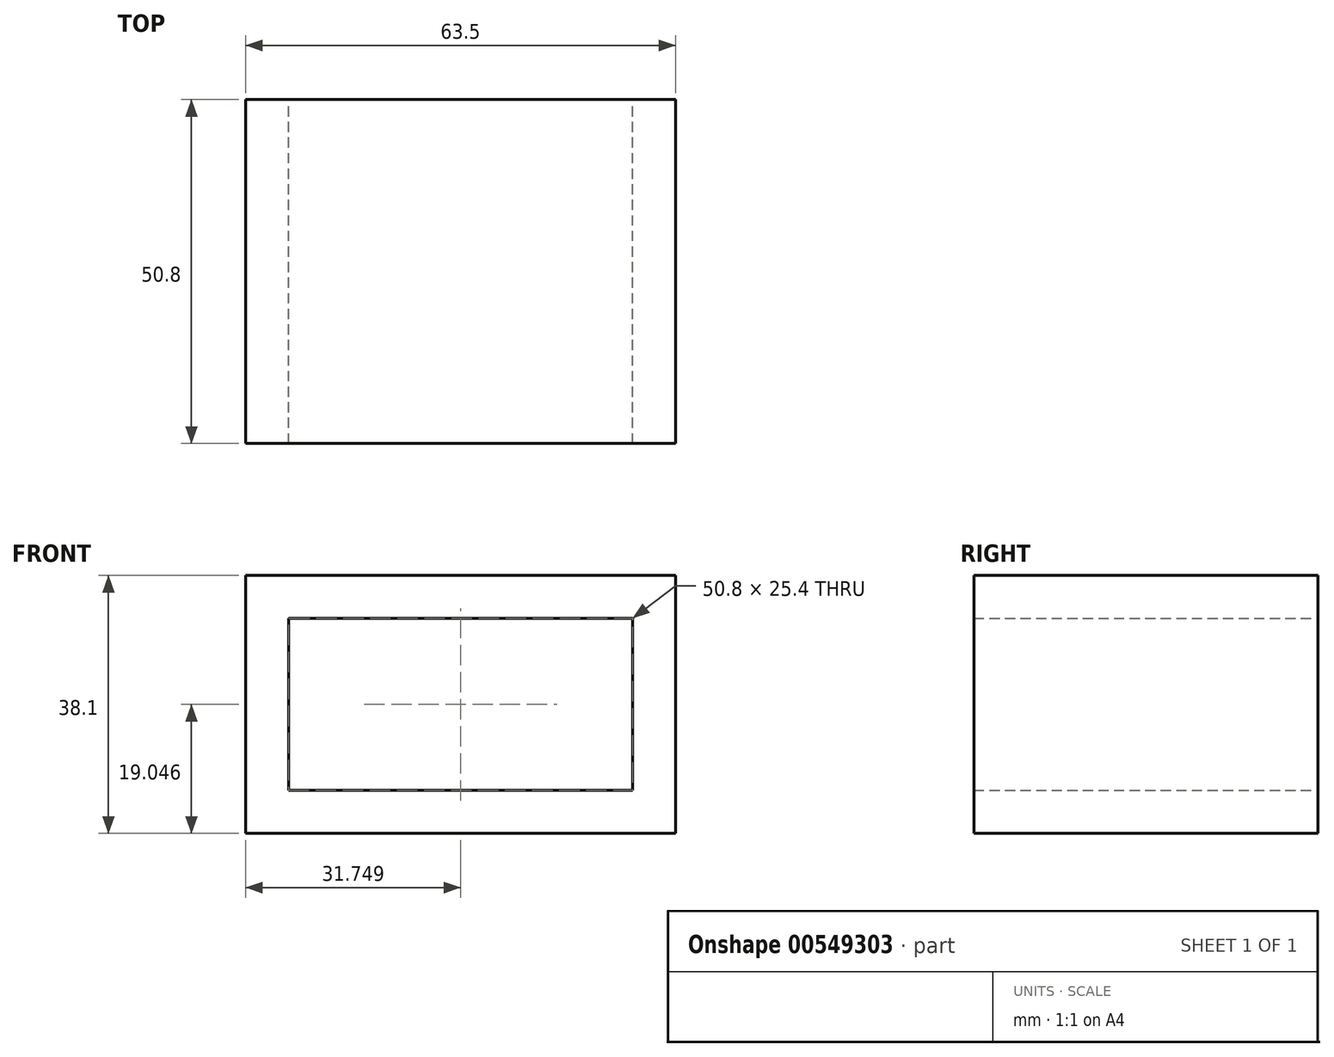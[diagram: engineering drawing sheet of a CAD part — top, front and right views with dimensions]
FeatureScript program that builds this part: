
annotation { "Feature Type Name" : "Feature", "Feature Type Description" : "" }
export const myFeature = defineFeature(function(context is Context, id is Id, definition is map)
    precondition{}
    {
        {
            var Q0;
            Q0=qCreatedBy(makeId("Front.planeOp"),FACE);
            var sketch = newSketch(context, id + "F0", { "sketchPlane" : qUnion([Q0])});
            skLineSegment(sketch, "E0.bottom", {"start": v(-36.81, 8.6) * mm, "end": v(-87.61, 8.6) * mm});
            skLineSegment(sketch, "E0.top", {"start": v(-36.81, 34) * mm, "end": v(-87.61, 34) * mm});
            skLineSegment(sketch, "E0.left", {"start": v(-36.81, 8.6) * mm, "end": v(-36.81, 34) * mm});
            skLineSegment(sketch, "E0.right", {"start": v(-87.61, 8.6) * mm, "end": v(-87.61, 34) * mm});
            skPoint(sketch, "E0.middle", {"position": v(-62.21, 21.3) * mm});
            skLineSegment(sketch, "E1.bottom", {"start": v(-30.46, 2.25) * mm, "end": v(-93.96, 2.25) * mm});
            skLineSegment(sketch, "E1.top", {"start": v(-30.46, 40.35) * mm, "end": v(-93.96, 40.35) * mm});
            skLineSegment(sketch, "E1.left", {"start": v(-30.46, 2.25) * mm, "end": v(-30.46, 40.35) * mm});
            skLineSegment(sketch, "E1.right", {"start": v(-93.96, 2.25) * mm, "end": v(-93.96, 40.35) * mm});
            skLineSegment(sketch, "E2", {"start": v(-93.96, 40.35) * mm, "end": v(-87.61, 34) * mm});
            skLineSegment(sketch, "E3", {"start": v(-36.81, 34) * mm, "end": v(-30.46, 40.35) * mm});
            skLineSegment(sketch, "E4", {"start": v(-36.81, 8.6) * mm, "end": v(-30.46, 2.25) * mm});
            skLineSegment(sketch, "E5", {"start": v(-87.61, 8.6) * mm, "end": v(-93.96, 2.25) * mm});
            skSolve(sketch);
        }
        {
            var Q0;
            Q0 = qSketchRegion(id + "F0", true);
            extrude(context, id + "F1", {"entities" : qUnion([Q0]), "depth" : 25.4 * mm, "offsetDistance" : 25.4 * mm});
        }
        {
            var Q0;
            Q0 = qSketchRegion(id + "F0", true);
            extrude(context, id + "F2", {"entities" : qUnion([Q0]), "operationType" : NewBodyOperationType.ADD, "oppositeDirection" : true, "depth" : 25.4 * mm, "offsetDistance" : 25.4 * mm});
        }
    });
